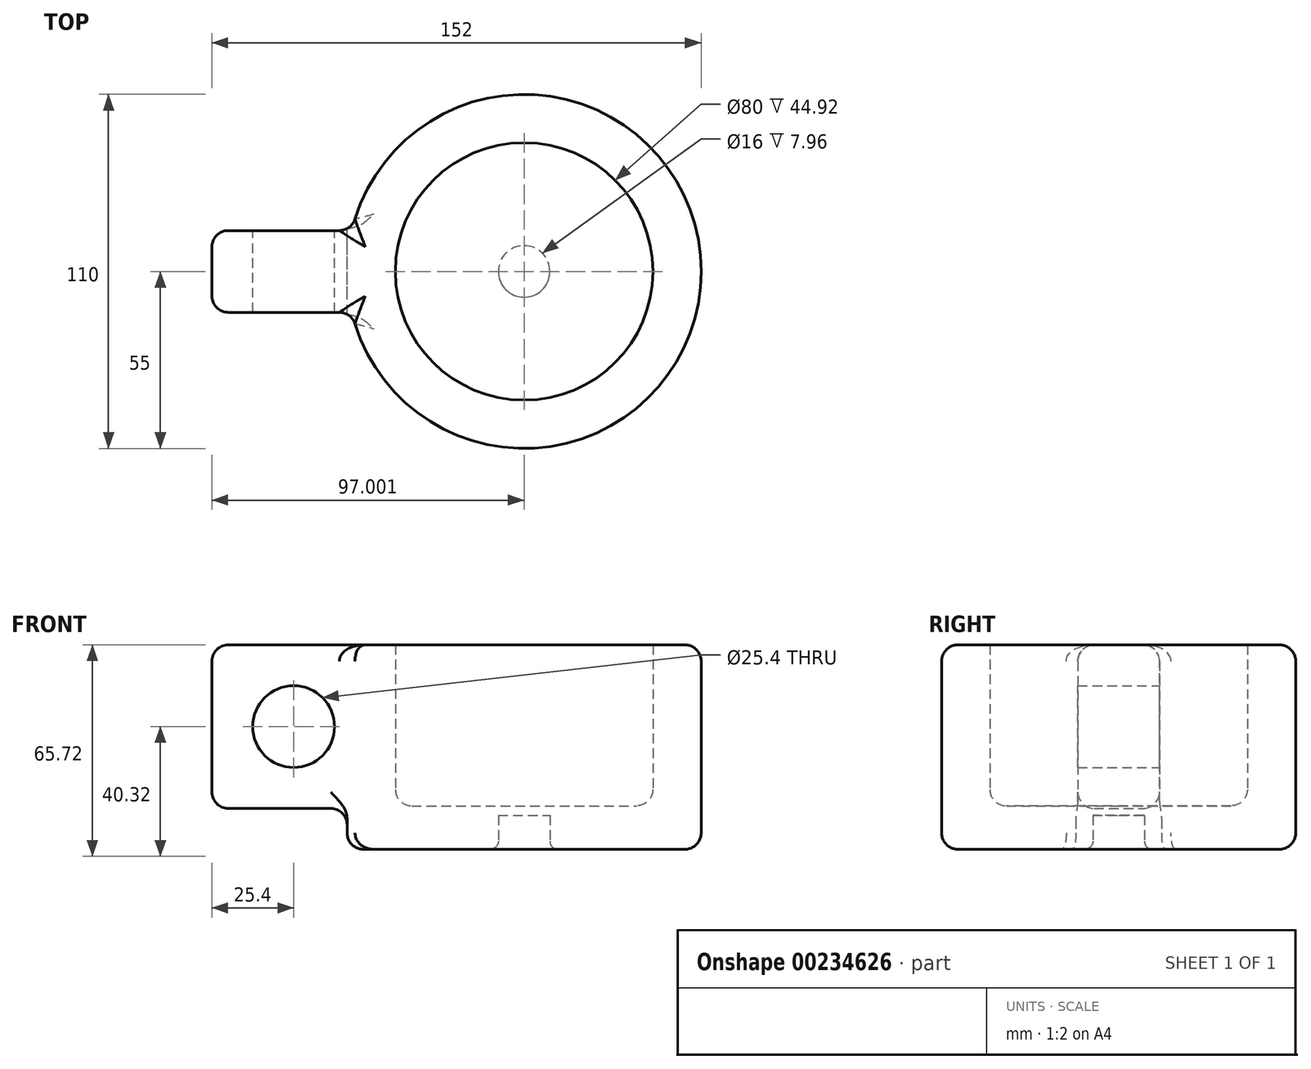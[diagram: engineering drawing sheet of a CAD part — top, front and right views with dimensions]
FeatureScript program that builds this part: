
annotation { "Feature Type Name" : "Feature", "Feature Type Description" : "" }
export const myFeature = defineFeature(function(context is Context, id is Id, definition is map)
    precondition{}
    {
        {
            var Q0;
            Q0=qCreatedBy(makeId("Front.planeOp"),FACE);
            var sketch = newSketch(context, id + "F0", { "sketchPlane" : qUnion([Q0])});
            skLineSegment(sketch, "E0.bottom", {"start": v(25.4, 25.4) * mm, "end": v(-25.4, 25.4) * mm});
            skLineSegment(sketch, "E0.top", {"start": v(25.4, -25.4) * mm, "end": v(-25.4, -25.4) * mm});
            skLineSegment(sketch, "E0.left", {"start": v(25.4, 25.4) * mm, "end": v(25.4, -25.4) * mm});
            skLineSegment(sketch, "E0.right", {"start": v(-25.4, 25.4) * mm, "end": v(-25.4, -25.4) * mm});
            skPoint(sketch, "E0.middle", {"position": v(0, 0) * mm});
            skCircle(sketch, "E1", {"center": v(0, 0) * mm, "radius": 12.7 * mm});
            skLineSegment(sketch, "E2", {"start": v(16.6, 25.4) * mm, "end": v(16.6, -38.1) * mm});
            skLineSegment(sketch, "E3", {"start": v(16.6, -38.1) * mm, "end": v(63.6, -38.1) * mm});
            skLineSegment(sketch, "E4", {"start": v(63.6, -38.1) * mm, "end": v(63.6, -27.6) * mm});
            skLineSegment(sketch, "E5", {"start": v(63.6, -27.6) * mm, "end": v(71.6, -27.6) * mm});
            skLineSegment(sketch, "E6", {"start": v(71.6, -27.6) * mm, "end": v(71.6, -24.6) * mm});
            skLineSegment(sketch, "E7", {"start": v(71.6, -24.6) * mm, "end": v(31.6, -24.6) * mm});
            skLineSegment(sketch, "E8", {"start": v(31.6, -24.6) * mm, "end": v(31.6, 25.4) * mm});
            skLineSegment(sketch, "E9", {"start": v(31.6, 25.4) * mm, "end": v(16.6, 25.4) * mm});
            skSolve(sketch);
        }
        {
            var Q0;
            {var subQ0=sQuery(id+"F0.wireOp",EDGE,"E0.left");Q0=makeQuery(id+"F0.imprint","IMPRINT",FACE,{"disambiguationData":[TD([[makeQuery(id+"F0.imprint","IMPRINT",EDGE,{"derivedFrom":subQ0}),-1.0]])]});}
            var Q1;
            {var subQ1=sQuery(id+"F0.wireOp",EDGE,"E0.left");Q1=makeQuery(id+"F0.imprint","IMPRINT",FACE,{"disambiguationData":[TD([[makeQuery(id+"F0.imprint","IMPRINT",EDGE,{"derivedFrom":subQ1}),1.0]])]});}
            var Q2;
            Q2=sQuery(id+"F0.wireOp",EDGE,"E6");
            revolve(context, id + "F1", {"entities" : qUnion([Q0, Q1]), "axis" : qUnion([Q2]), "revolveType" : RevolveType.FULL});
        }
        {
            var Q0;
            Q0 = qSketchRegion(id + "F0", true);
            extrude(context, id + "F2", {"entities" : qUnion([Q0]), "operationType" : NewBodyOperationType.ADD, "endBound" : BoundingType.SYMMETRIC, "depth" : 25.4 * mm});
        }
        {
            var Q0;
            Q0=makeQuery(id+"F2.opExtrude","CAP_EDGE",EDGE,{"disambiguationData":[OSD([sQuery(id+"F0.wireOp",EDGE,"E0.bottom"),sQuery(id+"F0.wireOp",EDGE,"E9")])],"isStart":false});
            fillet(context, id + "F3", {"entities" : qUnion([Q0]), "radius" : 5.08 * mm, "tangentPropagation" : true, "allowEdgeOverflow" : false});
        }
        {
            var Q0;
            Q0=makeQuery(id+"F2.opExtrude","CAP_EDGE",EDGE,{"disambiguationData":[OSD([sQuery(id+"F0.wireOp",EDGE,"E0.bottom"),sQuery(id+"F0.wireOp",EDGE,"E9")])],"isStart":true});
            var Q1;
            Q1=makeQuery(id+"F2.opExtrude","CAP_EDGE",EDGE,{"disambiguationData":[OSD([sQuery(id+"F0.wireOp",EDGE,"E0.right")])],"isStart":false});
            var Q2;
            Q2=makeQuery(id+"F2.opExtrude","CAP_EDGE",EDGE,{"disambiguationData":[OSD([sQuery(id+"F0.wireOp",EDGE,"E0.top")])],"isStart":false});
            var Q3;
            Q3=makeQuery(id+"F2.opExtrude","CAP_EDGE",EDGE,{"disambiguationData":[OSD([sQuery(id+"F0.wireOp",EDGE,"E0.top")])],"isStart":true});
            var Q4;
            Q4=makeQuery(id+"F1.opRevolve","SWEPT_EDGE",EDGE,{"disambiguationData":[OSD([sQuery(id+"F0.wireOp",EDGE,"E2"),sQuery(id+"F0.wireOp",EDGE,"E3")])]});
            var Q5;
            Q5=makeQuery(id+"F1.opRevolve","SWEPT_EDGE",EDGE,{"disambiguationData":[OSD([sQuery(id+"F0.wireOp",EDGE,"E0.bottom"),sQuery(id+"F0.wireOp",EDGE,"E2"),sQuery(id+"F0.wireOp",EDGE,"E9")])]});
            var Q6;
            Q6=makeQuery(id+"F1.opRevolve","SWEPT_EDGE",EDGE,{"disambiguationData":[OSD([sQuery(id+"F0.wireOp",EDGE,"E7"),sQuery(id+"F0.wireOp",EDGE,"E8")])]});
            fillet(context, id + "F4", {"entities" : qUnion([Q0, Q1, Q2, Q3, Q4, Q5, Q6]), "radius" : 5.08 * mm, "tangentPropagation" : true, "allowEdgeOverflow" : false});
        }
        {
            var Q0;
            Q0=makeQuery(id+"F1.opRevolve","SWEPT_EDGE",EDGE,{"disambiguationData":[OSD([sQuery(id+"F0.wireOp",EDGE,"E3"),sQuery(id+"F0.wireOp",EDGE,"E4")])]});
            fillet(context, id + "F5", {"entities" : qUnion([Q0]), "radius" : 2.54 * mm, "tangentPropagation" : true, "allowEdgeOverflow" : false});
        }
        {
            var Q0;
            Q0=makeQuery(id+"F2.opExtrude","SWEPT_EDGE",EDGE,{"disambiguationData":[OSD([sQuery(id+"F0.wireOp",EDGE,"E2"),sQuery(id+"F0.wireOp",EDGE,"E3")])]});
            var Q1;
            Q1=makeQuery(id+"F2.opExtrude","SWEPT_EDGE",EDGE,{"disambiguationData":[OSD([sQuery(id+"F0.wireOp",EDGE,"E0.top"),sQuery(id+"F0.wireOp",EDGE,"E2")])]});
            fillet(context, id + "F6", {"entities" : qUnion([Q0, Q1]), "radius" : 5.08 * mm, "tangentPropagation" : true, "allowEdgeOverflow" : false});
        }
        {
            var Q0;
            Q0=makeQuery(id+"F2.opExtrude","CAP_EDGE",EDGE,{"disambiguationData":[OSD([sQuery(id+"F0.wireOp",EDGE,"E0.right")])],"isStart":true});
            fillet(context, id + "F7", {"entities" : qUnion([Q0]), "radius" : 5.08 * mm, "tangentPropagation" : true, "allowEdgeOverflow" : false});
        }
        {
            var Q0;
            {var subQ0=sQuery(id+"F0.wireOp",EDGE,"E2");Q0=makeQuery(id+"F2.boolean.opBoolean","INTERSECT",EDGE,{"derivedFrom":[makeQuery(id+"F1.opRevolve","SWEPT_FACE",FACE,{"disambiguationData":[OSD([subQ0])]}),makeQuery(id+"F2.opExtrude","CAP_FACE",FACE,{"disambiguationData":[OSD([sQuery(id+"F0.wireOp",EDGE,"E0.bottom"),sQuery(id+"F0.wireOp",EDGE,"E0.top"),sQuery(id+"F0.wireOp",EDGE,"E0.right"),sQuery(id+"F0.wireOp",EDGE,"E1"),subQ0,sQuery(id+"F0.wireOp",EDGE,"E3"),sQuery(id+"F0.wireOp",EDGE,"E4"),sQuery(id+"F0.wireOp",EDGE,"E5"),sQuery(id+"F0.wireOp",EDGE,"E6"),sQuery(id+"F0.wireOp",EDGE,"E7"),sQuery(id+"F0.wireOp",EDGE,"E8"),sQuery(id+"F0.wireOp",EDGE,"E9")])],"isStart":false})]});}
            var Q1;
            {var subQ0=sQuery(id+"F0.wireOp",EDGE,"E2");Q1=makeQuery(id+"F2.boolean.opBoolean","INTERSECT",EDGE,{"derivedFrom":[makeQuery(id+"F1.opRevolve","SWEPT_FACE",FACE,{"disambiguationData":[OSD([subQ0])]}),makeQuery(id+"F2.opExtrude","CAP_FACE",FACE,{"disambiguationData":[OSD([sQuery(id+"F0.wireOp",EDGE,"E0.bottom"),sQuery(id+"F0.wireOp",EDGE,"E0.top"),sQuery(id+"F0.wireOp",EDGE,"E0.right"),sQuery(id+"F0.wireOp",EDGE,"E1"),subQ0,sQuery(id+"F0.wireOp",EDGE,"E3"),sQuery(id+"F0.wireOp",EDGE,"E4"),sQuery(id+"F0.wireOp",EDGE,"E5"),sQuery(id+"F0.wireOp",EDGE,"E6"),sQuery(id+"F0.wireOp",EDGE,"E7"),sQuery(id+"F0.wireOp",EDGE,"E8"),sQuery(id+"F0.wireOp",EDGE,"E9")])],"isStart":true})]});}
            fillet(context, id + "F8", {"entities" : qUnion([Q0, Q1]), "radius" : 5.08 * mm, "tangentPropagation" : true, "allowEdgeOverflow" : false});
        }
    });
